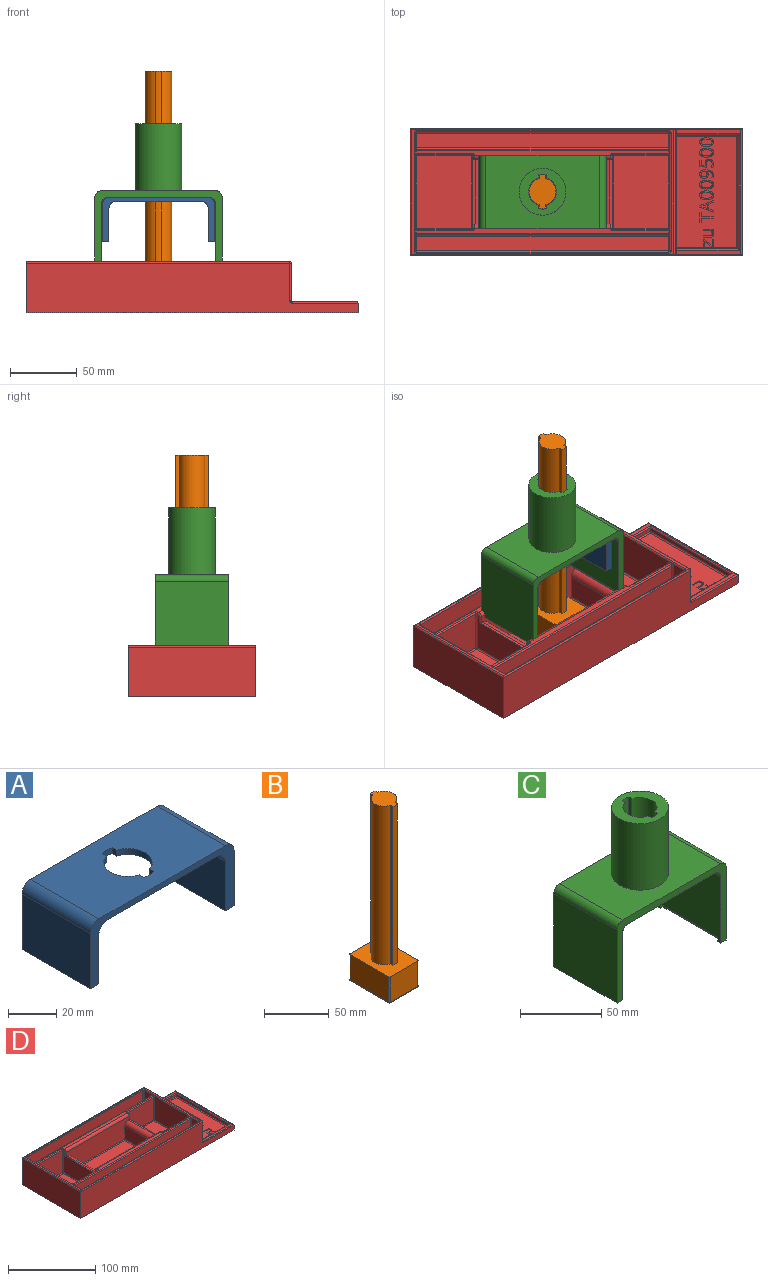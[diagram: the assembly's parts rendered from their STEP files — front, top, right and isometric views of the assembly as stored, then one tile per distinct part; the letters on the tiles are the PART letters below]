
ASSEMBLY  parts=4 mates=3
PART A: 22 faces, bbox 84x40x33 mm
  f0: plane 40x5mm, normal (0,0,-1), area 200mm2, adj f1,f7,f8,f9
  f1: plane 40x25mm, normal (1,0,0), area 1000mm2, adj f0,f8,f9,f18
  f2: plane 64x40mm, normal (0,0,-1), area 2215.5mm2, adj f8,f9,f10,f11,f12,f13,f14,f15
  f3: plane 40x25mm, normal (-1,0,0), area 1000mm2, adj f4,f8,f9,f19
  f4: plane 40x5mm, normal (0,0,-1), area 200mm2, adj f3,f5,f8,f9
  f5: plane 40x28mm, normal (1,0,0), area 1120mm2, adj f4,f8,f9,f20
  f6: plane 74x40mm, normal (0,0,1), area 2615.5mm2, adj f8,f9,f10,f11,f12,f13,f14,f15
  f7: plane 40x28mm, normal (-1,0,0), area 1120mm2, adj f0,f8,f9,f21
  f8: plane 84x33mm, normal (0,-1,0), area 552mm2, adj f0,f1,f2,f3,f4,f5,f6,f7
  f9: plane 84x33mm, normal (0,1,0), area 552mm2, adj f0,f1,f2,f3,f4,f5,f6,f7
  f10: plane 3x2.6mm, normal (1,0,0), area 7.8mm2, adj f2,f6,f11,f17
  f11: cylinder r=12.5mm len=6mm, axis (0,0,1), area 18.2mm2, adj f2,f6,f10,f12
  f12: plane 3x2.6mm, normal (-1,0,0), area 7.8mm2, adj f2,f6,f11,f13
  f13: cylinder r=10mm len=19.08mm, axis (0,0,1), area 76mm2, adj f2,f6,f12,f14
  f14: plane 3x2.6mm, normal (-1,0,0), area 7.8mm2, adj f2,f6,f13,f15
  f15: cylinder r=12.5mm len=6mm, axis (0,0,1), area 18.2mm2, adj f2,f6,f14,f16
  f16: plane 3x2.6mm, normal (1,0,0), area 7.8mm2, adj f2,f6,f15,f17
  f17: cylinder r=10mm len=19.08mm, axis (0,0,1), area 76mm2, adj f2,f6,f10,f16
  f18: cylinder r=5mm len=40mm, axis (0,1,0), area 314.2mm2, adj f1,f2,f8,f9
  f19: cylinder r=5mm len=40mm, axis (0,-1,0), area 314.2mm2, adj f2,f3,f8,f9
  f20: cylinder r=5mm len=40mm, axis (0,-1,0), area 314.2mm2, adj f5,f6,f8,f9
  f21: cylinder r=5mm len=40mm, axis (0,1,0), area 314.2mm2, adj f6,f7,f8,f9
PART B: 27 faces, bbox 32x44x175 mm
  f0: cylinder r=12.5mm len=150mm, axis (0,0,-1), area 755.1mm2, adj f2,f7,f23,f26
  f1: cylinder r=12.5mm len=150mm, axis (0,0,-1), area 755.1mm2, adj f2,f7,f21,f24
  f2: plane 25x20mm, normal (0,0,1), area 339.4mm2, adj f0,f1,f21,f22,f23,f24,f25,f26
  f3: plane 30x24mm, normal (0,1,0), area 720mm2, adj f7,f14,f18,f20
  f4: plane 42x24mm, normal (-1,0,0), area 1008mm2, adj f7,f11,f17,f20
  f5: plane 30x24mm, normal (0,-1,0), area 720mm2, adj f7,f9,f11,f12
  f6: plane 42x24mm, normal (1,0,0), area 1008mm2, adj f7,f9,f13,f14
  f7: plane 44x32mm, normal (0,0,1), area 1067.8mm2, adj f0,f1,f3,f4,f5,f6,f9,f11
  f8: plane 42x30mm, normal (0,0,-1), area 1260mm2, adj f12,f13,f17,f18
  f9: cylinder r=1mm len=24mm, axis (0,0,1), area 37.7mm2, adj f5,f6,f7,f10
  f10: sphere r=1mm, area 1.6mm2, adj f9,f12,f13
  f11: cylinder r=1mm len=24mm, axis (0,0,-1), area 37.7mm2, adj f4,f5,f7,f15
  f12: cylinder r=1mm len=30mm, axis (1,0,0), area 47.1mm2, adj f5,f8,f10,f15
  f13: cylinder r=1mm len=42mm, axis (0,1,0), area 66mm2, adj f6,f8,f10,f16
  f14: cylinder r=1mm len=24mm, axis (0,0,-1), area 37.7mm2, adj f3,f6,f7,f16
  f15: sphere r=1mm, area 1.6mm2, adj f11,f12,f17
  f16: sphere r=1mm, area 1.6mm2, adj f13,f14,f18
  f17: cylinder r=1mm len=42mm, axis (0,-1,0), area 66mm2, adj f4,f8,f15,f19
  f18: cylinder r=1mm len=30mm, axis (-1,0,0), area 47.1mm2, adj f3,f8,f16,f19
  f19: sphere r=1mm, area 1.6mm2, adj f17,f18,f20
  f20: cylinder r=1mm len=24mm, axis (0,0,1), area 37.7mm2, adj f3,f4,f7,f19
  f21: plane 150x2.57mm, normal (1,0,0), area 384.7mm2, adj f1,f2,f7,f22
  f22: cylinder r=10mm len=150mm, axis (0,0,1), area 3954.3mm2, adj f2,f7,f21,f23
  f23: plane 150x2.57mm, normal (1,0,0), area 384.7mm2, adj f0,f2,f7,f22
  f24: plane 150x2.57mm, normal (-1,0,0), area 384.7mm2, adj f1,f2,f7,f25
  f25: cylinder r=10mm len=150mm, axis (0,0,1), area 3954.3mm2, adj f2,f7,f24,f26
  f26: plane 150x2.57mm, normal (-1,0,0), area 384.7mm2, adj f0,f2,f7,f25
PART C: 34 faces, bbox 95x55x110 mm
  f0: plane 55x50mm, normal (1,0,0), area 2600mm2, adj f1,f4,f5,f6,f7,f8,f28
  f1: plane 55x4.75mm, normal (0,0,-1), area 148.8mm2, adj f0,f3,f4,f5,f6,f7,f9
  f2: plane 85x55mm, normal (0,0,1), area 3712.9mm2, adj f4,f5,f30,f31,f32
  f3: plane 55x55mm, normal (-1,0,0), area 3025mm2, adj f1,f4,f5,f30
  f4: plane 95x60mm, normal (0,-1,0), area 997.5mm2, adj f0,f1,f2,f3,f11,f12,f13,f14
  f5: plane 95x60mm, normal (0,1,0), area 997.5mm2, adj f0,f1,f2,f3,f11,f12,f13,f14
  f6: plane 3x2.25mm, normal (0,1,0), area 5.9mm2, adj f0,f1,f8,f9,f10
  f7: plane 3x2.25mm, normal (0,-1,0), area 5.9mm2, adj f0,f1,f8,f9,f10
  f8: plane 50x0.25mm, normal (0,0,-1), area 12.5mm2, adj f0,f6,f7,f10
  f9: plane 50x1mm, normal (1,0,0), area 50mm2, adj f1,f6,f7,f10
  f10: cylinder r=2mm len=50mm, axis (0,1,0), area 157.1mm2, adj f6,f7,f8,f9
  f11: plane 75.5x55mm, normal (0,0,-1), area 3775.8mm2, adj f4,f5,f20,f21,f22,f23,f24,f25
  f12: plane 55x50mm, normal (-1,0,0), area 2600mm2, adj f4,f5,f13,f15,f16,f18,f29
  f13: plane 55x4.75mm, normal (0,0,-1), area 148.8mm2, adj f4,f5,f12,f14,f15,f16,f17
  f14: plane 55x55mm, normal (1,0,0), area 3025mm2, adj f4,f5,f13,f31
  f15: plane 3x2.25mm, normal (0,1,0), area 5.9mm2, adj f12,f13,f17,f18,f19
  f16: plane 3x2.25mm, normal (0,-1,0), area 5.9mm2, adj f12,f13,f17,f18,f19
  f17: plane 50x1mm, normal (-1,0,0), area 50mm2, adj f13,f15,f16,f19
  f18: plane 50x0.25mm, normal (0,0,-1), area 12.5mm2, adj f12,f15,f16,f19
  f19: cylinder r=2mm len=50mm, axis (0,-1,0), area 157.1mm2, adj f15,f16,f17,f18
  f20: cylinder r=13mm len=55mm, axis (0,0,1), area 333mm2, adj f11,f21,f27,f33
  f21: plane 55x2.59mm, normal (-1,0,0), area 142.3mm2, adj f11,f20,f22,f33
  f22: cylinder r=10.5mm len=55mm, axis (0,0,1), area 1479.6mm2, adj f11,f21,f23,f33
  f23: plane 55x2.59mm, normal (-1,0,0), area 142.3mm2, adj f11,f22,f24,f33
  f24: cylinder r=13mm len=55mm, axis (0,0,1), area 333mm2, adj f11,f23,f25,f33
  f25: plane 55x2.59mm, normal (1,0,0), area 142.3mm2, adj f11,f24,f26,f33
  f26: cylinder r=10.5mm len=55mm, axis (0,0,1), area 1479.6mm2, adj f11,f25,f27,f33
  f27: plane 55x2.59mm, normal (1,0,0), area 142.3mm2, adj f11,f20,f26,f33
  f28: cylinder r=5mm len=55mm, axis (0,-1,0), area 432mm2, adj f0,f4,f5,f11
  f29: cylinder r=5mm len=55mm, axis (0,1,0), area 432mm2, adj f4,f5,f11,f12
  f30: cylinder r=5mm len=55mm, axis (0,-1,0), area 432mm2, adj f2,f3,f4,f5
  f31: cylinder r=5mm len=55mm, axis (0,1,0), area 432mm2, adj f2,f4,f5,f14
  f32: cylinder r=17.5mm len=50mm, axis (0,0,-1), area 5497.8mm2, adj f2,f33
  f33: plane 35x35mm, normal (0,0,1), area 585.4mm2, adj f20,f21,f22,f23,f24,f25,f26,f27
PART D: 336 faces, bbox 248x95x38 mm
  f0: plane 33x13mm, normal (1,0,0), area 363.9mm2, adj f289,f300,f309,f313,f314
  f1: plane 58x33mm, normal (1,0,0), area 1783.7mm2, adj f281,f295,f305,f313,f317,f320
  f2: plane 33x13mm, normal (-1,0,0), area 363.9mm2, adj f260,f261,f270,f278,f279
  f3: plane 58x33mm, normal (-1,0,0), area 1783.7mm2, adj f252,f253,f257,f267,f279,f280
  f4: plane 188x4mm, normal (0,0,1), area 581.7mm2, adj f239,f247,f251,f266,f282,f283,f293,f306
  f5: plane 188x4mm, normal (0,0,1), area 581.7mm2, adj f238,f259,f268,f292,f310,f318,f322,f323
  f6: plane 83x45mm, normal (0,0,1), area 3362.4mm2, adj f41,f44,f46,f47,f72,f73,f74,f75
  f7: plane 50x2mm, normal (0,0,1), area 96.4mm2, adj f24,f32,f34,f63,f265,f324
  f8: plane 33x13mm, normal (-1,0,0), area 363.9mm2, adj f274,f275,f279,f291,f302
  f9: plane 50x2mm, normal (0,0,1), area 96.4mm2, adj f24,f28,f34,f64,f240,f246
  f10: plane 93x33mm, normal (1,0,0), area 3020.7mm2, adj f42,f45,f46,f49,f50,f54,f57,f59
  f11: plane 188x11mm, normal (0,0,1), area 2068mm2, adj f260,f262,f272,f273
  f12: plane 54x41mm, normal (0,0,1), area 2214mm2, adj f304,f305,f315,f316
  f13: plane 188x11mm, normal (0,0,1), area 2068mm2, adj f274,f276,f289,f290
  f14: plane 54x41mm, normal (0,0,1), area 2214mm2, adj f244,f245,f253,f254
  f15: plane 248x37mm, normal (0,1,0), area 7646.9mm2, adj f16,f18,f36,f50,f53,f56,f326
  f16: plane 95x37mm, normal (-1,0,0), area 3515mm2, adj f15,f17,f18,f327
  f17: plane 248x37mm, normal (0,-1,0), area 7646.9mm2, adj f16,f18,f36,f60,f61,f62,f329
  f18: plane 248x95mm, normal (0,0,-1), area 23560mm2, adj f15,f16,f17,f36
  f19: plane 33x13mm, normal (1,0,0), area 363.9mm2, adj f272,f284,f296,f297,f313
  f20: plane 188x33mm, normal (0,-1,0), area 6204mm2, adj f275,f276,f299,f300
  f21: plane 188x33mm, normal (0,1,0), area 6204mm2, adj f273,f278,f297,f298
  f22: plane 196x93mm, normal (0,0,1), area 567.4mm2, adj f279,f286,f287,f298,f299,f307,f308,f313
  f23: plane 48x18mm, normal (1,0,0), area 864mm2, adj f24,f34,f63,f333
  f24: plane 102x29mm, normal (0,-1,0), area 2637.5mm2, adj f7,f9,f23,f25,f63,f64,f238,f246
  f25: plane 48x18mm, normal (-1,0,0), area 864mm2, adj f24,f34,f64,f334
  f26: plane 188x31mm, normal (0,-1,0), area 5828mm2, adj f261,f262,f283,f284
  f27: plane 41x31mm, normal (0,1,0), area 1271mm2, adj f243,f244,f251,f252
  f28: plane 54x31mm, normal (1,0,0), area 1322.3mm2, adj f9,f240,f241,f243,f245,f246,f250,f255
  f29: plane 41x31mm, normal (0,-1,0), area 1271mm2, adj f254,f255,f267,f268
  f30: plane 188x31mm, normal (0,1,0), area 5828mm2, adj f290,f291,f309,f310
  f31: plane 41x31mm, normal (0,-1,0), area 1271mm2, adj f316,f317,f321,f322
  f32: plane 54x31mm, normal (-1,0,0), area 1322.3mm2, adj f7,f265,f269,f303,f315,f321,f324,f325
  f33: plane 41x31mm, normal (0,1,0), area 1271mm2, adj f281,f282,f303,f304
  f34: plane 102x29mm, normal (0,1,0), area 2637.5mm2, adj f7,f9,f23,f25,f63,f64,f239,f240
  f35: plane 86x46mm, normal (0,0,1), area 3956mm2, adj f332,f333,f334,f335
  f36: plane 95x7mm, normal (1,0,0), area 665mm2, adj f15,f17,f18,f58
  f37: plane 46x3mm, normal (0,-1,0), area 138mm2, adj f38,f41,f42,f48
  f38: plane 85x3mm, normal (-1,0,0), area 255mm2, adj f37,f39,f44,f52
  f39: plane 46x3mm, normal (0,1,0), area 138mm2, adj f38,f47,f54,f55
  f40: plane 93x48mm, normal (0,0,1), area 375mm2, adj f48,f49,f52,f55,f56,f58,f59,f60
  f41: cylinder r=1mm len=46mm, axis (1,0,0), area 71.7mm2, adj f6,f37,f43,f44
  f42: cylinder r=1mm len=3mm, axis (0,0,-1), area 4.7mm2, adj f10,f37,f43,f45
  f43: sphere r=1mm, area 1.6mm2, adj f41,f42,f46
  f44: cylinder r=1mm len=85mm, axis (0,-1,0), area 132.4mm2, adj f6,f38,f41,f47
  f45: torus R=2mm, axis (1,0,0), area 3.4mm2, adj f10,f42,f48,f49
  f46: cylinder r=1mm len=83mm, axis (0,-1,0), area 130.4mm2, adj f6,f10,f43,f51
  f47: cylinder r=1mm len=46mm, axis (-1,0,0), area 71.7mm2, adj f6,f39,f44,f51
  f48: cylinder r=1mm len=47mm, axis (-1,0,0), area 72.8mm2, adj f37,f40,f45,f52
  f49: cylinder r=1mm len=3mm, axis (0,-1,0), area 4.7mm2, adj f10,f40,f45,f53
  f50: cylinder r=1mm len=28mm, axis (0,0,-1), area 44mm2, adj f10,f15,f53,f328
  f51: sphere r=1mm, area 1.6mm2, adj f46,f47,f54
  f52: cylinder r=1mm len=87mm, axis (0,1,0), area 134.7mm2, adj f38,f40,f48,f55
  f53: torus R=2mm, axis (0,1,0), area 3.4mm2, adj f15,f49,f50,f56
  f54: cylinder r=1mm len=3mm, axis (0,0,-1), area 4.7mm2, adj f10,f39,f51,f57
  f55: cylinder r=1mm len=47mm, axis (1,0,0), area 72.8mm2, adj f39,f40,f52,f57
  f56: cylinder r=1mm len=49mm, axis (-1,0,0), area 76.4mm2, adj f15,f40,f53,f58
  f57: torus R=2mm, axis (1,0,0), area 3.4mm2, adj f10,f54,f55,f59
  f58: cylinder r=1mm len=95mm, axis (0,1,0), area 148.1mm2, adj f36,f40,f56,f60
  f59: cylinder r=1mm len=3mm, axis (0,-1,0), area 4.7mm2, adj f10,f40,f57,f61
  f60: cylinder r=1mm len=49mm, axis (1,0,0), area 76.4mm2, adj f17,f40,f58,f61
  f61: torus R=2mm, axis (0,1,0), area 3.4mm2, adj f17,f59,f60,f62
  f62: cylinder r=1mm len=28mm, axis (0,0,1), area 44mm2, adj f10,f17,f61,f331
  f63: cylinder r=6mm len=48mm, axis (0,-1,0), area 452.4mm2, adj f7,f23,f24,f34
  f64: cylinder r=6mm len=48mm, axis (0,1,0), area 452.4mm2, adj f9,f24,f25,f34
  f65: extruded ~3.15x2mm, area 6.4mm2, adj f66,f80,f81,f232
  f66: extruded ~3.14x2mm, area 6.4mm2, adj f65,f67,f81,f232
  f67: extruded ~2x1.62mm, area 4mm2, adj f66,f68,f81,f232
  f68: extruded ~2x1.63mm, area 4mm2, adj f67,f69,f81,f232
  f69: extruded ~3.13x2mm, area 6.4mm2, adj f68,f70,f81,f232
  f70: extruded ~3.14x2mm, area 6.4mm2, adj f69,f71,f81,f232
  f71: extruded ~2x1.63mm, area 4.1mm2, adj f70,f80,f81,f232
  f72: extruded ~3.84x2mm, area 7.9mm2, adj f6,f73,f79,f81
  f73: extruded ~3.79x2mm, area 7.9mm2, adj f6,f72,f74,f81
  f74: extruded ~2.45x2mm, area 5.8mm2, adj f6,f73,f75,f81
  f75: extruded ~2.46x2mm, area 5.8mm2, adj f6,f74,f76,f81
  f76: extruded ~3.84x2mm, area 8mm2, adj f6,f75,f77,f81
  f77: extruded ~3.81x2mm, area 7.9mm2, adj f6,f76,f78,f81
  f78: extruded ~2.43x2mm, area 5.8mm2, adj f6,f77,f79,f81
  f79: extruded ~2.48x2mm, area 5.8mm2, adj f6,f72,f78,f81
  f80: extruded ~2x1.62mm, area 4mm2, adj f65,f71,f81,f232
  f81: plane 10.21x6.56mm, normal (0,0,1), area 26mm2, adj f65,f66,f67,f68,f69,f70,f71,f72
  f82: plane 4.82x2mm, normal (0,-1,0), area 9.6mm2, adj f6,f83,f98,f99
  f83: plane 2x1.14mm, normal (1,0,0), area 2.3mm2, adj f6,f82,f84,f99
  f84: plane 4.86x2mm, normal (0,1,0), area 9.7mm2, adj f6,f83,f85,f99
  f85: extruded ~2.06x2mm, area 4.5mm2, adj f6,f84,f86,f99
  f86: extruded ~2.03x2mm, area 4.4mm2, adj f6,f85,f87,f99
  f87: extruded ~2x1.4mm, area 2.9mm2, adj f6,f86,f88,f99
  f88: extruded ~2x0.96mm, area 2.6mm2, adj f6,f87,f89,f99
  f89: plane 2x0.06mm, normal (-1,0,0), area 0.1mm2, adj f6,f88,f90,f99
  f90: plane 2x1mm, normal (-0.16,0.99,0), area 2mm2, adj f6,f89,f91,f99
  f91: plane 2x0.93mm, normal (-1,0,0), area 1.9mm2, adj f6,f90,f92,f99
  f92: plane 7.43x2mm, normal (0,-1,0), area 14.9mm2, adj f6,f91,f93,f99
  f93: plane 2x1.13mm, normal (1,0,0), area 2.3mm2, adj f6,f92,f94,f99
  f94: plane 3.91x2mm, normal (0,1,0), area 7.8mm2, adj f6,f93,f95,f99
  f95: extruded ~2.08x2mm, area 4.4mm2, adj f6,f94,f96,f99
  f96: extruded ~2x1.71mm, area 3.8mm2, adj f6,f95,f97,f99
  f97: extruded ~2x1.29mm, area 2.8mm2, adj f6,f96,f98,f99
  f98: extruded ~2x1.36mm, area 2.9mm2, adj f6,f82,f97,f99
  f99: plane 7.57x6.22mm, normal (0,0,1), area 20.1mm2, adj f82,f83,f84,f85,f86,f87,f88,f89
  f100: plane 2x1.15mm, normal (-1,0,0), area 2.3mm2, adj f6,f101,f107,f108
  f101: plane 8.89x2mm, normal (0,-1,0), area 17.8mm2, adj f6,f100,f102,f108
  f102: plane 3.14x2mm, normal (-1,0,0), area 6.3mm2, adj f6,f101,f103,f108
  f103: plane 2x1.02mm, normal (0,-1,0), area 2mm2, adj f6,f102,f104,f108
  f104: plane 7.43x2mm, normal (1,0,0), area 14.9mm2, adj f6,f103,f105,f108
  f105: plane 2x1.02mm, normal (0,1,0), area 2mm2, adj f6,f104,f106,f108
  f106: plane 3.14x2mm, normal (-1,0,0), area 6.3mm2, adj f6,f105,f107,f108
  f107: plane 8.89x2mm, normal (0,1,0), area 17.8mm2, adj f6,f100,f106,f108
  f108: plane 9.92x7.43mm, normal (0,0,1), area 17.9mm2, adj f100,f101,f102,f103,f104,f105,f106,f107
  f109: extruded ~2.47x2mm, area 5.3mm2, adj f6,f110,f127,f128
  f110: extruded ~2x1.55mm, area 3.1mm2, adj f6,f109,f111,f128
  f111: plane 2.98x2mm, normal (-0.08,-1,0), area 6mm2, adj f6,f110,f112,f128
  f112: plane 3.97x2mm, normal (-1,0,0), area 7.9mm2, adj f6,f111,f113,f128
  f113: plane 2x1.04mm, normal (0,-1,0), area 2.1mm2, adj f6,f112,f114,f128
  f114: plane 4.93x2mm, normal (1,0,0), area 9.9mm2, adj f6,f113,f115,f128
  f115: plane 4.64x2mm, normal (0.08,1,0), area 9.3mm2, adj f6,f114,f116,f128
  f116: plane 2x0.58mm, normal (-0.84,0.54,0), area 1.4mm2, adj f6,f115,f117,f128
  f117: extruded ~2x1.72mm, area 3.5mm2, adj f6,f116,f118,f128
  f118: extruded ~2.54x2.07mm, area 7.5mm2, adj f6,f117,f119,f128
  f119: extruded ~2x1.63mm, area 3.6mm2, adj f6,f118,f120,f128
  f120: extruded ~2x1.85mm, area 4mm2, adj f6,f119,f121,f128
  f121: extruded ~2x1.39mm, area 2.8mm2, adj f6,f120,f122,f128
  f122: extruded ~2x1.18mm, area 2.6mm2, adj f6,f121,f123,f128
  f123: plane 2x1.09mm, normal (0,1,0), area 2.2mm2, adj f6,f122,f124,f128
  f124: extruded ~2.56x2mm, area 5.3mm2, adj f6,f123,f125,f128
  f125: extruded ~2.7x2mm, area 5.8mm2, adj f6,f124,f126,f128
  f126: extruded ~2.41x2mm, area 5.4mm2, adj f6,f125,f127,f128
  f127: extruded ~2.13x2mm, area 4.8mm2, adj f6,f109,f126,f128
  f128: plane 10.05x6.24mm, normal (0,0,1), area 22.8mm2, adj f109,f110,f111,f112,f113,f114,f115,f116
  f129: plane 3.07x2mm, normal (-0.35,0.94,0), area 6.6mm2, adj f130,f141,f142,f233
  f130: plane 3.21x2mm, normal (1,0,0), area 6.4mm2, adj f129,f131,f142,f233
  f131: plane 3.07x2mm, normal (-0.35,-0.94,0), area 6.6mm2, adj f130,f132,f142,f233
  f132: extruded ~2x1.43mm, area 3mm2, adj f131,f141,f142,f233
  f133: plane 3.15x2mm, normal (-0.36,0.93,0), area 6.8mm2, adj f6,f134,f140,f142
  f134: plane 2x1.19mm, normal (-1,0,0), area 2.4mm2, adj f6,f133,f135,f142
  f135: plane 9.96x3.9mm, normal (0.36,-0.93,0), area 21.4mm2, adj f6,f134,f136,f142
  f136: plane 2x0.97mm, normal (1,0,0), area 1.9mm2, adj f6,f135,f137,f142
  f137: plane 9.96x3.92mm, normal (0.37,0.93,0), area 21.4mm2, adj f6,f136,f138,f142
  f138: plane 2x1.17mm, normal (-1,0,0), area 2.3mm2, adj f6,f137,f139,f142
  f139: plane 3.15x2mm, normal (-0.36,-0.93,0), area 6.8mm2, adj f6,f138,f140,f142
  f140: plane 3.97x2mm, normal (-1,0,0), area 7.9mm2, adj f6,f133,f139,f142
  f141: extruded ~2x1.43mm, area 3mm2, adj f129,f132,f142,f233
  f142: plane 9.96x8.79mm, normal (0,0,1), area 25.3mm2, adj f129,f130,f131,f132,f133,f134,f135,f136
  f143: extruded ~3.15x2mm, area 6.4mm2, adj f144,f158,f159,f234
  f144: extruded ~3.14x2mm, area 6.4mm2, adj f143,f145,f159,f234
  f145: extruded ~2x1.62mm, area 4mm2, adj f144,f146,f159,f234
  f146: extruded ~2x1.63mm, area 4mm2, adj f145,f147,f159,f234
  f147: extruded ~3.13x2mm, area 6.4mm2, adj f146,f148,f159,f234
  f148: extruded ~3.14x2mm, area 6.4mm2, adj f147,f149,f159,f234
  f149: extruded ~2x1.63mm, area 4.1mm2, adj f148,f158,f159,f234
  f150: extruded ~3.84x2mm, area 7.9mm2, adj f6,f151,f157,f159
  f151: extruded ~3.79x2mm, area 7.9mm2, adj f6,f150,f152,f159
  f152: extruded ~2.45x2mm, area 5.8mm2, adj f6,f151,f153,f159
  f153: extruded ~2.46x2mm, area 5.8mm2, adj f6,f152,f154,f159
  f154: extruded ~3.84x2mm, area 8mm2, adj f6,f153,f155,f159
  f155: extruded ~3.81x2mm, area 7.9mm2, adj f6,f154,f156,f159
  f156: extruded ~2.43x2mm, area 5.8mm2, adj f6,f155,f157,f159
  f157: extruded ~2.48x2mm, area 5.8mm2, adj f6,f150,f156,f159
  f158: extruded ~2x1.62mm, area 4mm2, adj f143,f149,f159,f234
  f159: plane 10.21x6.56mm, normal (0,0,1), area 26mm2, adj f143,f144,f145,f146,f147,f148,f149,f150
  f160: extruded ~3.15x2mm, area 6.4mm2, adj f161,f175,f176,f235
  f161: extruded ~3.14x2mm, area 6.4mm2, adj f160,f162,f176,f235
  f162: extruded ~2x1.62mm, area 4mm2, adj f161,f163,f176,f235
  f163: extruded ~2x1.63mm, area 4mm2, adj f162,f164,f176,f235
  f164: extruded ~3.13x2mm, area 6.4mm2, adj f163,f165,f176,f235
  f165: extruded ~3.14x2mm, area 6.4mm2, adj f164,f166,f176,f235
  f166: extruded ~2x1.63mm, area 4.1mm2, adj f165,f175,f176,f235
  f167: extruded ~3.84x2mm, area 7.9mm2, adj f6,f168,f174,f176
  f168: extruded ~3.79x2mm, area 7.9mm2, adj f6,f167,f169,f176
  f169: extruded ~2.45x2mm, area 5.8mm2, adj f6,f168,f170,f176
  f170: extruded ~2.46x2mm, area 5.8mm2, adj f6,f169,f171,f176
  f171: extruded ~3.84x2mm, area 8mm2, adj f6,f170,f172,f176
  f172: extruded ~3.81x2mm, area 7.9mm2, adj f6,f171,f173,f176
  f173: extruded ~2.43x2mm, area 5.8mm2, adj f6,f172,f174,f176
  f174: extruded ~2.48x2mm, area 5.8mm2, adj f6,f167,f173,f176
  f175: extruded ~2x1.62mm, area 4mm2, adj f160,f166,f176,f235
  f176: plane 10.21x6.56mm, normal (0,0,1), area 26mm2, adj f160,f161,f162,f163,f164,f165,f166,f167
  f177: extruded ~2x1.5mm, area 3.4mm2, adj f178,f202,f203,f236
  f178: extruded ~2x1.14mm, area 2.4mm2, adj f177,f179,f203,f236
  f179: extruded ~2x0.95mm, area 2.5mm2, adj f178,f180,f203,f236
  f180: extruded ~2x1.32mm, area 2.7mm2, adj f179,f181,f203,f236
  f181: extruded ~2x0.91mm, area 1.9mm2, adj f180,f182,f203,f236
  f182: extruded ~2x0.82mm, area 2.2mm2, adj f181,f183,f203,f236
  f183: extruded ~2x1.14mm, area 2.3mm2, adj f182,f184,f203,f236
  f184: extruded ~2x1.48mm, area 3.3mm2, adj f183,f185,f203,f236
  f185: extruded ~2x1.54mm, area 3.3mm2, adj f184,f202,f203,f236
  f186: extruded ~5.82x4.5mm, area 16.8mm2, adj f6,f187,f201,f203
  f187: extruded ~2.34x2mm, area 4.8mm2, adj f6,f186,f188,f203
  f188: extruded ~2x1.51mm, area 3.9mm2, adj f6,f187,f189,f203
  f189: extruded ~2x1.77mm, area 3.7mm2, adj f6,f188,f190,f203
  f190: extruded ~2.28x2mm, area 5mm2, adj f6,f189,f191,f203
  f191: extruded ~2.44x2mm, area 5.3mm2, adj f6,f190,f192,f203
  f192: extruded ~2.2x2mm, area 4.8mm2, adj f6,f191,f193,f203
  f193: extruded ~2.09x2mm, area 4.6mm2, adj f6,f192,f194,f203
  f194: extruded ~2x1.39mm, area 2.9mm2, adj f6,f193,f195,f203
  f195: extruded ~2x0.99mm, area 2.7mm2, adj f6,f194,f196,f203
  f196: plane 2x0.08mm, normal (-1,0,0), area 0.2mm2, adj f6,f195,f197,f203
  f197: extruded ~3.09x2mm, area 6.5mm2, adj f6,f196,f198,f203
  f198: extruded ~2.46x2mm, area 5.5mm2, adj f6,f197,f199,f203
  f199: extruded ~2x1.23mm, area 2.5mm2, adj f6,f198,f200,f203
  f200: plane 2x0.97mm, normal (0,1,0), area 1.9mm2, adj f6,f199,f201,f203
  f201: extruded ~2x1.25mm, area 2.5mm2, adj f6,f186,f200,f203
  f202: extruded ~2x1.74mm, area 3.7mm2, adj f177,f185,f203,f236
  f203: plane 10.19x6.48mm, normal (0,0,1), area 25.5mm2, adj f177,f178,f179,f180,f181,f182,f183,f184
  f204: extruded ~3.15x2mm, area 6.4mm2, adj f205,f219,f220,f237
  f205: extruded ~3.14x2mm, area 6.4mm2, adj f204,f206,f220,f237
  f206: extruded ~2x1.62mm, area 4mm2, adj f205,f207,f220,f237
  f207: extruded ~2x1.63mm, area 4mm2, adj f206,f208,f220,f237
  f208: extruded ~3.13x2mm, area 6.4mm2, adj f207,f209,f220,f237
  f209: extruded ~3.14x2mm, area 6.4mm2, adj f208,f210,f220,f237
  f210: extruded ~2x1.63mm, area 4.1mm2, adj f209,f219,f220,f237
  f211: extruded ~3.84x2mm, area 7.9mm2, adj f6,f212,f218,f220
  f212: extruded ~3.79x2mm, area 7.9mm2, adj f6,f211,f213,f220
  f213: extruded ~2.45x2mm, area 5.8mm2, adj f6,f212,f214,f220
  f214: extruded ~2.46x2mm, area 5.8mm2, adj f6,f213,f215,f220
  f215: extruded ~3.84x2mm, area 8mm2, adj f6,f214,f216,f220
  f216: extruded ~3.81x2mm, area 7.9mm2, adj f6,f215,f217,f220
  f217: extruded ~2.43x2mm, area 5.8mm2, adj f6,f216,f218,f220
  f218: extruded ~2.48x2mm, area 5.8mm2, adj f6,f211,f217,f220
  f219: extruded ~2x1.62mm, area 4mm2, adj f204,f210,f220,f237
  f220: plane 10.21x6.56mm, normal (0,0,1), area 26mm2, adj f204,f205,f206,f207,f208,f209,f210,f211
  f221: plane 5.39x2mm, normal (-1,0,0), area 10.8mm2, adj f6,f222,f230,f231
  f222: plane 2x0.87mm, normal (0,-1,0), area 1.7mm2, adj f6,f221,f223,f231
  f223: plane 4.1x2mm, normal (1,0,0), area 8.2mm2, adj f6,f222,f224,f231
  f224: plane 5.68x4mm, normal (-0.58,-0.82,0), area 13.9mm2, adj f6,f223,f225,f231
  f225: plane 2x0.87mm, normal (0,-1,0), area 1.7mm2, adj f6,f224,f226,f231
  f226: plane 5.04x2mm, normal (1,0,0), area 10.1mm2, adj f6,f225,f227,f231
  f227: plane 2x0.87mm, normal (0,1,0), area 1.7mm2, adj f6,f226,f228,f231
  f228: plane 3.8x2mm, normal (-1,0,0), area 7.6mm2, adj f6,f227,f229,f231
  f229: plane 5.79x4.06mm, normal (0.57,0.82,0), area 14.1mm2, adj f6,f228,f230,f231
  f230: plane 2x0.77mm, normal (0,1,0), area 1.5mm2, adj f6,f221,f229,f231
  f231: plane 7.43x5.39mm, normal (0,0,1), area 16.1mm2, adj f221,f222,f223,f224,f225,f226,f227,f228
  f232: plane 8.26x4.26mm, normal (0,0,1), area 29.8mm2, adj f65,f66,f67,f68,f69,f70,f71,f80
  f233: plane 4.5x3.21mm, normal (0,0,1), area 6.9mm2, adj f129,f130,f131,f132,f141
  f234: plane 8.26x4.26mm, normal (0,0,1), area 29.8mm2, adj f143,f144,f145,f146,f147,f148,f149,f158
  f235: plane 8.26x4.26mm, normal (0,0,1), area 29.8mm2, adj f160,f161,f162,f163,f164,f165,f166,f175
  f236: plane 4.46x4.23mm, normal (0,0,1), area 15.2mm2, adj f177,f178,f179,f180,f181,f182,f183,f184
  f237: plane 8.26x4.26mm, normal (0,0,1), area 29.8mm2, adj f204,f205,f206,f207,f208,f209,f210,f219
  f238: cylinder r=3mm len=102mm, axis (-1,0,0), area 480.7mm2, adj f5,f24,f250,f325
  f239: cylinder r=3mm len=102mm, axis (1,0,0), area 480.7mm2, adj f4,f34,f241,f269
  f240: cylinder r=1mm len=5mm, axis (0,0,-1), area 7.9mm2, adj f9,f28,f34,f241
  f241: torus R=2mm, axis (1,0,0), area 6.5mm2, adj f28,f239,f240,f247
  f242: sphere r=1mm, area 1.6mm2, adj f243,f244,f245
  f243: cylinder r=1mm len=31mm, axis (0,0,-1), area 48.7mm2, adj f27,f28,f242,f247
  f244: cylinder r=1mm len=41mm, axis (-1,0,0), area 64.4mm2, adj f14,f27,f242,f248
  f245: cylinder r=1mm len=54mm, axis (0,1,0), area 84.8mm2, adj f14,f28,f242,f249
  f246: cylinder r=1mm len=5mm, axis (0,0,1), area 7.9mm2, adj f9,f24,f28,f250
  f247: torus R=2mm, axis (0,0,1), area 3.4mm2, adj f4,f241,f243,f251
  f248: sphere r=1mm, area 1.6mm2, adj f244,f252,f253
  f249: sphere r=1mm, area 1.6mm2, adj f245,f254,f255
  f250: torus R=2mm, axis (1,0,0), area 6.5mm2, adj f28,f238,f246,f259
  f251: cylinder r=1mm len=41mm, axis (1,0,0), area 64.4mm2, adj f4,f27,f247,f257
  f252: cylinder r=1mm len=31mm, axis (0,0,1), area 48.7mm2, adj f3,f27,f248,f257
  f253: cylinder r=1mm len=54mm, axis (0,-1,0), area 84.8mm2, adj f3,f14,f248,f258
  f254: cylinder r=1mm len=41mm, axis (1,0,0), area 64.4mm2, adj f14,f29,f249,f258
  f255: cylinder r=1mm len=31mm, axis (0,0,-1), area 48.7mm2, adj f28,f29,f249,f259
  f256: sphere r=1mm, area 1.6mm2, adj f260,f261,f262
  f257: torus R=2mm, axis (1,0,0), area 3.4mm2, adj f3,f251,f252,f266
  f258: sphere r=1mm, area 1.6mm2, adj f253,f254,f267
  f259: torus R=2mm, axis (0,0,1), area 3.4mm2, adj f5,f250,f255,f268
  f260: cylinder r=1mm len=11mm, axis (0,-1,0), area 17.3mm2, adj f2,f11,f256,f264
  f261: cylinder r=1mm len=31mm, axis (0,0,-1), area 48.7mm2, adj f2,f26,f256,f270
  f262: cylinder r=1mm len=188mm, axis (1,0,0), area 295.3mm2, adj f11,f26,f256,f271
  f263: sphere r=1mm, area 1.6mm2, adj f274,f275,f276
  f264: sphere r=1mm, area 1.6mm2, adj f260,f273,f278
  f265: cylinder r=1mm len=5mm, axis (0,0,1), area 7.9mm2, adj f7,f32,f34,f269
  f266: cylinder r=1mm len=2mm, axis (0,-1,0), area 3.1mm2, adj f4,f257,f270,f279
  f267: cylinder r=1mm len=31mm, axis (0,0,1), area 48.7mm2, adj f3,f29,f258,f280
  f268: cylinder r=1mm len=41mm, axis (-1,0,0), area 64.4mm2, adj f5,f29,f259,f280
  f269: torus R=2mm, axis (1,0,0), area 6.5mm2, adj f32,f239,f265,f293
  f270: torus R=2mm, axis (1,0,0), area 3.4mm2, adj f2,f261,f266,f283
  f271: sphere r=1mm, area 1.6mm2, adj f262,f272,f284
  f272: cylinder r=1mm len=11mm, axis (0,1,0), area 17.3mm2, adj f11,f19,f271,f285
  f273: cylinder r=1mm len=188mm, axis (-1,0,0), area 295.3mm2, adj f11,f21,f264,f285
  f274: cylinder r=1mm len=11mm, axis (0,-1,0), area 17.3mm2, adj f8,f13,f263,f277
  f275: cylinder r=1mm len=33mm, axis (0,0,1), area 51.8mm2, adj f8,f20,f263,f287
  f276: cylinder r=1mm len=188mm, axis (1,0,0), area 295.3mm2, adj f13,f20,f263,f288
  f277: sphere r=1mm, area 1.6mm2, adj f274,f290,f291
  f278: cylinder r=1mm len=33mm, axis (0,0,-1), area 51.8mm2, adj f2,f21,f264,f286
  f279: cylinder r=1mm len=88mm, axis (0,1,0), area 138.2mm2, adj f2,f3,f8,f22,f266,f286,f287,f292
  f280: torus R=2mm, axis (1,0,0), area 3.4mm2, adj f3,f267,f268,f292
  f281: cylinder r=1mm len=31mm, axis (0,0,1), area 48.7mm2, adj f1,f33,f294,f295
  f282: cylinder r=1mm len=41mm, axis (1,0,0), area 64.4mm2, adj f4,f33,f293,f295
  f283: cylinder r=1mm len=188mm, axis (-1,0,0), area 295.3mm2, adj f4,f26,f270,f296
  f284: cylinder r=1mm len=31mm, axis (0,0,1), area 48.7mm2, adj f19,f26,f271,f296
  f285: sphere r=1mm, area 1.6mm2, adj f272,f273,f297
  f286: torus R=2mm, axis (0,0,1), area 3.4mm2, adj f22,f278,f279,f298
  f287: torus R=2mm, axis (0,0,1), area 3.4mm2, adj f22,f275,f279,f299
  f288: sphere r=1mm, area 1.6mm2, adj f276,f289,f300
  f289: cylinder r=1mm len=11mm, axis (0,1,0), area 17.3mm2, adj f0,f13,f288,f301
  f290: cylinder r=1mm len=188mm, axis (-1,0,0), area 295.3mm2, adj f13,f30,f277,f301
  f291: cylinder r=1mm len=31mm, axis (0,0,1), area 48.7mm2, adj f8,f30,f277,f302
  f292: cylinder r=1mm len=2mm, axis (0,-1,0), area 3.1mm2, adj f5,f279,f280,f302
  f293: torus R=2mm, axis (0,0,1), area 3.4mm2, adj f4,f269,f282,f303
  f294: sphere r=1mm, area 1.6mm2, adj f281,f304,f305
  f295: torus R=2mm, axis (1,0,0), area 3.4mm2, adj f1,f281,f282,f306
  f296: torus R=2mm, axis (1,0,0), area 3.4mm2, adj f19,f283,f284,f306
  f297: cylinder r=1mm len=33mm, axis (0,0,1), area 51.8mm2, adj f19,f21,f285,f307
  f298: cylinder r=1mm len=188mm, axis (1,0,0), area 295.3mm2, adj f21,f22,f286,f307
  f299: cylinder r=1mm len=188mm, axis (-1,0,0), area 295.3mm2, adj f20,f22,f287,f308
  f300: cylinder r=1mm len=33mm, axis (0,0,-1), area 51.8mm2, adj f0,f20,f288,f308
  f301: sphere r=1mm, area 1.6mm2, adj f289,f290,f309
  f302: torus R=2mm, axis (1,0,0), area 3.4mm2, adj f8,f291,f292,f310
  f303: cylinder r=1mm len=31mm, axis (0,0,-1), area 48.7mm2, adj f32,f33,f293,f311
  f304: cylinder r=1mm len=41mm, axis (-1,0,0), area 64.4mm2, adj f12,f33,f294,f311
  f305: cylinder r=1mm len=54mm, axis (0,1,0), area 84.8mm2, adj f1,f12,f294,f312
  f306: cylinder r=1mm len=2mm, axis (0,1,0), area 3.1mm2, adj f4,f295,f296,f313
  f307: torus R=2mm, axis (0,0,1), area 3.4mm2, adj f22,f297,f298,f313
  f308: torus R=2mm, axis (0,0,1), area 3.4mm2, adj f22,f299,f300,f313
  f309: cylinder r=1mm len=31mm, axis (0,0,-1), area 48.7mm2, adj f0,f30,f301,f314
  f310: cylinder r=1mm len=188mm, axis (1,0,0), area 295.3mm2, adj f5,f30,f302,f314
  f311: sphere r=1mm, area 1.6mm2, adj f303,f304,f315
  f312: sphere r=1mm, area 1.6mm2, adj f305,f316,f317
  f313: cylinder r=1mm len=88mm, axis (0,-1,0), area 138.2mm2, adj f0,f1,f19,f22,f306,f307,f308,f318
  f314: torus R=2mm, axis (1,0,0), area 3.4mm2, adj f0,f309,f310,f318
  f315: cylinder r=1mm len=54mm, axis (0,-1,0), area 84.8mm2, adj f12,f32,f311,f319
  f316: cylinder r=1mm len=41mm, axis (1,0,0), area 64.4mm2, adj f12,f31,f312,f319
  f317: cylinder r=1mm len=31mm, axis (0,0,-1), area 48.7mm2, adj f1,f31,f312,f320
  f318: cylinder r=1mm len=2mm, axis (0,1,0), area 3.1mm2, adj f5,f313,f314,f320
  f319: sphere r=1mm, area 1.6mm2, adj f315,f316,f321
  f320: torus R=2mm, axis (1,0,0), area 3.4mm2, adj f1,f317,f318,f322
  f321: cylinder r=1mm len=31mm, axis (0,0,1), area 48.7mm2, adj f31,f32,f319,f323
  f322: cylinder r=1mm len=41mm, axis (-1,0,0), area 64.4mm2, adj f5,f31,f320,f323
  f323: torus R=2mm, axis (0,0,1), area 3.4mm2, adj f5,f321,f322,f325
  f324: cylinder r=1mm len=5mm, axis (0,0,-1), area 7.9mm2, adj f7,f24,f32,f325
  f325: torus R=2mm, axis (1,0,0), area 6.5mm2, adj f32,f238,f323,f324
  f326: cylinder r=1mm len=197mm, axis (1,0,0), area 308.9mm2, adj f15,f22,f327,f328
  f327: cylinder r=1mm len=95mm, axis (0,1,0), area 148.1mm2, adj f16,f22,f326,f329
  f328: sphere r=1mm, area 1.6mm2, adj f50,f326,f330
  f329: cylinder r=1mm len=197mm, axis (-1,0,0), area 308.9mm2, adj f17,f22,f327,f331
  f330: cylinder r=1mm len=93mm, axis (0,-1,0), area 146.1mm2, adj f10,f22,f328,f331
  f331: sphere r=1mm, area 1.6mm2, adj f62,f329,f330
  f332: cylinder r=1mm len=88mm, axis (1,0,0), area 137.1mm2, adj f24,f35,f333,f334
  f333: cylinder r=1mm len=48mm, axis (0,1,0), area 74.3mm2, adj f23,f35,f332,f335
  f334: cylinder r=1mm len=48mm, axis (0,-1,0), area 74.3mm2, adj f25,f35,f332,f335
  f335: cylinder r=1mm len=88mm, axis (-1,0,0), area 137.1mm2, adj f34,f35,f333,f334
PLACE A rot(axis=(0,0,1),180deg) t=(98,47.5,52.95)mm
PLACE B t=(98,47.5,5.11)mm
PLACE C t=(98,47.5,30.95)mm
PLACE D t=(98,47.5,0)mm
MATE slider D.f35 <-> B.f0  axis (0,0,1) through (98,47.5,3)mm
MATE slider C.f26 <-> B.f22  axis (0,0,-1) through (98,47.5,85.95)mm
MATE slider B.f22 <-> A.f13  axis (0,0,1) through (98,47.5,30.11)mm
